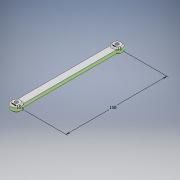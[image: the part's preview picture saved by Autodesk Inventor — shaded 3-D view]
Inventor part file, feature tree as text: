
AUTODESK INVENTOR PART (.ipt)
format: ipt  version: 2018 (Build 220112000, 112)  size: 125,440 bytes
history: native  units: mm
features: extrude x2, other x1, sketch x1, chamfer x1
ambient origin geometry x8: Origin, YZ Plane, XZ Plane, XY Plane, X Axis, Y Axis, Z Axis, Center Point
bodies: Body1 (feature_tree)
feature tree (5):
  other  "Твердое тело1"
  sketch  "Эскиз1"
  extrude  "Выдавливание1"  Depth=15.0mm
  extrude  "Выдавливание2"  Depth=15.0mm
  chamfer  "Фаска1"  Distance=5.0mm
